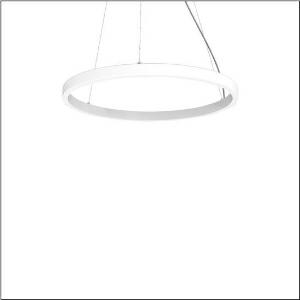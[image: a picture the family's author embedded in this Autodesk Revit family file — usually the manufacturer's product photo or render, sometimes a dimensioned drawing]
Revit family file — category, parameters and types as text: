
# Revit family: silica_r__21_ring-o_5pjbo3d1004a_d373
name_source: partatom
category: Lighting Fixtures
units: mm (PartAtom-declared; Revit-internal decimal feet)

## family parameters
Cut with Voids When Loaded = No
Host = Face
Light Source = No
Part Type = Normal
Room Calculation Point = No
Round Connector Dimension = Use Diameter
Shared = No

## types (1)
- Silica® 21 Ring-O (1 x LED, 6860 lm, 105 W, 3000K)
    Apparent Load = 105 VA
    CIE Flux Codes = 2 16 49 50 100
    Color Rendering = 80
    Color Temperature = 3000K
    Default Elevation = 1800 mm
    Description = Silica® 21 Ring-O, suspended luminaire, of PMMA, frosted, light emission: outer ring side luminous distribution, primary light characteristic: symmetric, installation type: suspended mounting, LED, rated luminous flux: 6.860lm, luminous efficacy: 65lm/W, light colour: 830, colour temperature: 3000K, control gear: DALI 2, with terminal, 5-pole, mains connection: 230V, AC/DC, 0/50..60Hz, rated input power: 105W, housing, of extruded aluminium section, traffic white (RAL 9016), diameter: 1.100mm, ceiling canopy, traffic white (RAL 9016), protection rating (lamp compartment): IP40, insulation class (complete): insulation class I (protective earthing), certification: CE, impact resistance: IK02, permissible operating ambient temperature: 0..+35°C, packaging unit: 1 piece
    Height = 48 mm  [stored 0.15748 ft]
    Lamp = 1 x LED
    Lamp Light Flux = 6860 lm
    Lamp Power = 105 W
    Lamp count = 1
    Length = 1100 mm
    Luminous efficacy = 65 lm/W
    Manufacturer = Siteco
    ModVariant = No
    Model = 5PJBO3D1004A
    Mounting Place = Ceiling
    Mounting Type = Pendant
    Number of Poles = 1
    OnlyDefault = Yes
    Power Factor = 1
    Product Name = Silica® 21 Ring-O
    Product group = suspended luminaire
    ProductGroupID = 905
    Protection Class = Protection class I
    Protection Degree = IP 40
    RLX_Detail_Level = 1
    RLX_Emergency_Light_Flux = 0 lm
    RLX_Emergency_Type = 0
    RLX_Emergency_Type_DB = No
    RlxData = <blob elided: 13545 chars, md5=f544baa5>
    Socket = socket
    Standby Power = 0 W
    System Light Flux = 6860 lm
    System Power = 105 W
    Type Comments = Product without accessories
    Type Image = l_1258387.jpg
    URL = http://relux.com
    VarID = ---
    Voltage = 0 V
    Weight = 0.00 kg
    Width = 0 mm  [stored 0 ft]

note: [stored X ft] marks values corroborated as IEEE doubles in the binary element streams (Revit-internal decimal feet)

## geometry (parser evidence)
native form markers: Sweep x12
no freeform markers — native parametric forms only
